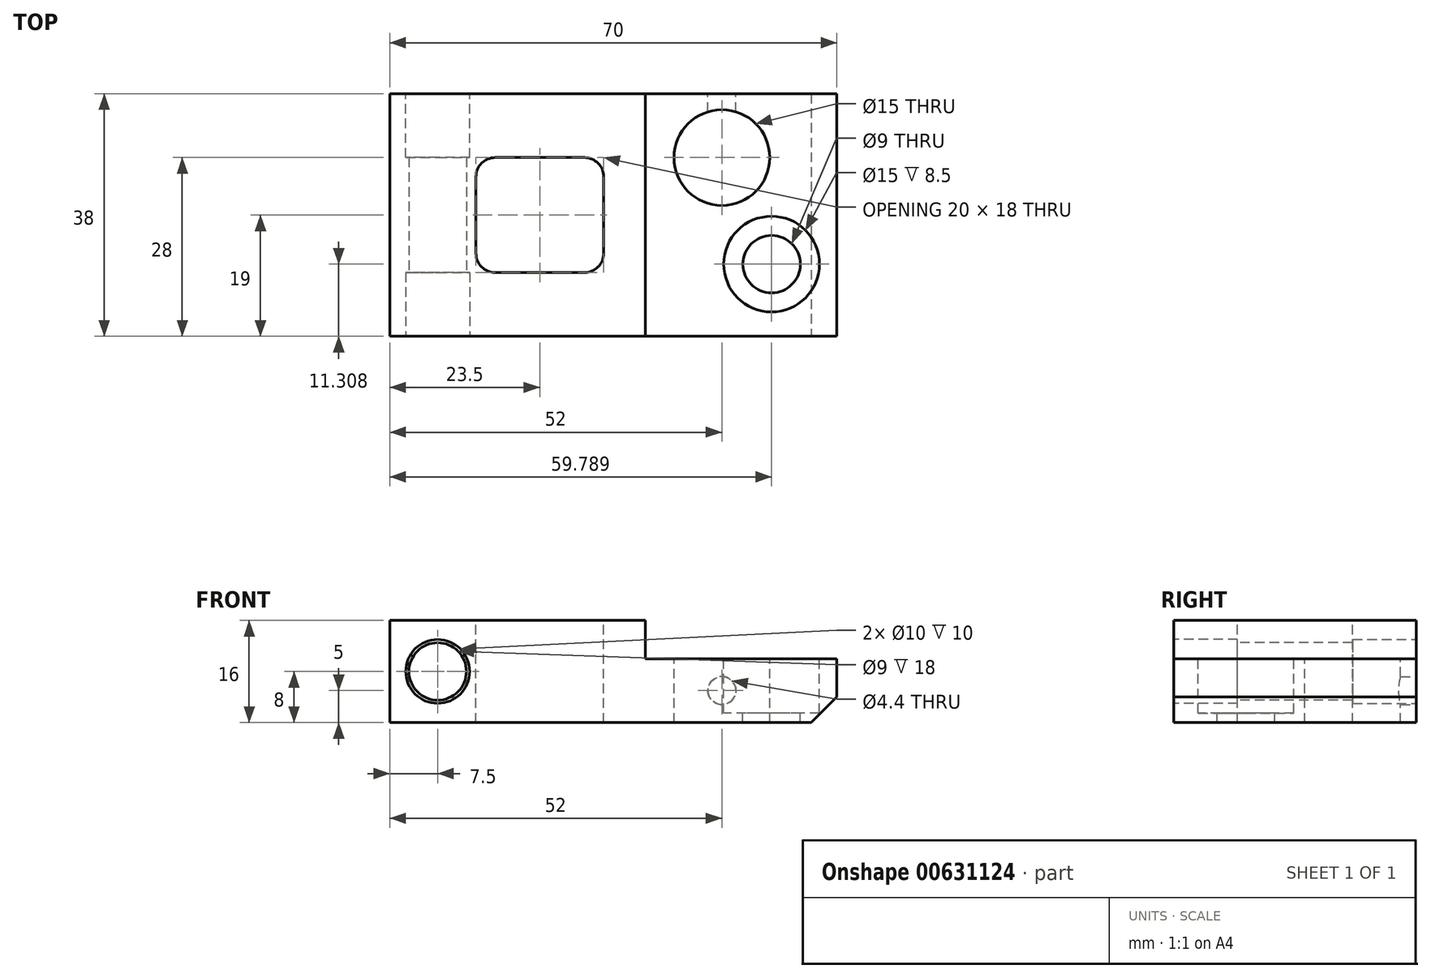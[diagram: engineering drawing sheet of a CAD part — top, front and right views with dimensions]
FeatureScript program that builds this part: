
annotation { "Feature Type Name" : "Feature", "Feature Type Description" : "" }
export const myFeature = defineFeature(function(context is Context, id is Id, definition is map)
    precondition{}
    {
        {
            var Q0;
            Q0=qCreatedBy(makeId("Top.planeOp"),FACE);
            var sketch = newSketch(context, id + "F0", { "sketchPlane" : qUnion([Q0])});
            skLineSegment(sketch, "E0.bottom", {"start": v(-35, 19) * mm, "end": v(35, 19) * mm});
            skLineSegment(sketch, "E0.top", {"start": v(-35, -19) * mm, "end": v(35, -19) * mm});
            skLineSegment(sketch, "E0.left", {"start": v(-35, 19) * mm, "end": v(-35, -19) * mm});
            skLineSegment(sketch, "E0.right", {"start": v(35, 19) * mm, "end": v(35, -19) * mm});
            skSolve(sketch);
        }
        {
            var Q0;
            Q0=makeQuery(id+"F0.imprint","IMPRINT",FACE,{"disambiguationData":[TD([[makeQuery(id+"F0.imprint","IMPRINT",EDGE,{"derivedFrom":sQuery(id+"F0.wireOp",EDGE,"E0.bottom")}),-1.0]])]});
            extrude(context, id + "F1", {"entities" : qUnion([Q0]), "depth" : 16 * mm, "offsetDistance" : 25 * mm});
        }
        {
            var Q0;
            Q0=makeQuery(id+"F1.opExtrude","SWEPT_FACE",FACE,{"disambiguationData":[OSD([sQuery(id+"F0.wireOp",EDGE,"E0.top")])]});
            var sketch = newSketch(context, id + "F2", { "sketchPlane" : qUnion([Q0])});
            skPoint(sketch, "E1", {"position": v(-27.5, 8) * mm});
            skSolve(sketch);
        }
        {
            var Q0;
            Q0=sQuery(id+"F2.wireOp",VERTEX,"E1");
            var Q1;
            Q1=makeQuery(id+"F1.opExtrude","SWEPT_BODY",BODY,{"disambiguationData":[OSD([sQuery(id+"F0.wireOp",EDGE,"E0.bottom"),sQuery(id+"F0.wireOp",EDGE,"E0.top"),sQuery(id+"F0.wireOp",EDGE,"E0.left"),sQuery(id+"F0.wireOp",EDGE,"E0.right")])]});
            hole(context, id + "F3", {"style" : HoleStyle.C_BORE, "endStyle" : HoleEndStyle.BLIND, "holeDiameter" : 9 * mm, "cBoreDiameter" : 10 * mm, "cBoreDepth" : 10 * mm, "majorDiameter" : 4 * mm, "holeDepth" : 28 * mm, "isTappedThrough" : true, "tappedDepth" : 11.5 * mm, "tapClearance" : 3, "locations" : qUnion([Q0]), "scope" : qUnion([Q1])});
        }
        {
            var Q0;
            Q0=makeQuery(id+"F1.opExtrude","SWEPT_FACE",FACE,{"disambiguationData":[OSD([sQuery(id+"F0.wireOp",EDGE,"E0.bottom")])]});
            var sketch = newSketch(context, id + "F4", { "sketchPlane" : qUnion([Q0])});
            skPoint(sketch, "E2", {"position": v(27.5, 8) * mm});
            skSolve(sketch);
        }
        {
            var Q0;
            Q0=sQuery(id+"F4.wireOp",VERTEX,"E2");
            var Q1;
            Q1=makeQuery(id+"F1.opExtrude","SWEPT_BODY",BODY,{"disambiguationData":[OSD([sQuery(id+"F0.wireOp",EDGE,"E0.bottom"),sQuery(id+"F0.wireOp",EDGE,"E0.top"),sQuery(id+"F0.wireOp",EDGE,"E0.left"),sQuery(id+"F0.wireOp",EDGE,"E0.right")])]});
            hole(context, id + "F5", {"style" : HoleStyle.C_BORE, "endStyle" : HoleEndStyle.BLIND, "holeDiameter" : 9 * mm, "cBoreDiameter" : 10 * mm, "cBoreDepth" : 10 * mm, "majorDiameter" : 5 * mm, "holeDepth" : 28 * mm, "isTappedThrough" : true, "tappedDepth" : 11.5 * mm, "tapClearance" : 3, "locations" : qUnion([Q0]), "scope" : qUnion([Q1])});
        }
        {
            var Q0;
            Q0=makeQuery(id+"F1.opExtrude","CAP_FACE",FACE,{"disambiguationData":[OSD([sQuery(id+"F0.wireOp",EDGE,"E0.bottom"),sQuery(id+"F0.wireOp",EDGE,"E0.top"),sQuery(id+"F0.wireOp",EDGE,"E0.left"),sQuery(id+"F0.wireOp",EDGE,"E0.right")])],"isStart":false});
            var sketch = newSketch(context, id + "F6", { "sketchPlane" : qUnion([Q0])});
            skLineSegment(sketch, "E3.bottom", {"start": v(-18.5, 9) * mm, "end": v(-4.5, 9) * mm});
            skLineSegment(sketch, "E3.top", {"start": v(-18.5, -9) * mm, "end": v(-4.5, -9) * mm});
            skLineSegment(sketch, "E3.left", {"start": v(-21.5, 6) * mm, "end": v(-21.5, -6) * mm});
            skLineSegment(sketch, "E3.right", {"start": v(-1.5, 6) * mm, "end": v(-1.5, -6) * mm});
            skPoint(sketch, "E4.visualSharp", {"position": v(-21.5, 9) * mm});
            skArc(sketch, "E4.filletArc", {"start": v(-18.5, 9) * mm, "mid": v(-20.62, 8.12) * mm, "end": v(-21.5, 6) * mm});
            skPoint(sketch, "E5.visualSharp", {"position": v(-21.5, -9) * mm});
            skArc(sketch, "E5.filletArc", {"start": v(-21.5, -6) * mm, "mid": v(-20.62, -8.12) * mm, "end": v(-18.5, -9) * mm});
            skPoint(sketch, "E6.visualSharp", {"position": v(-1.5, 9) * mm});
            skArc(sketch, "E6.filletArc", {"start": v(-1.5, 6) * mm, "mid": v(-2.38, 8.12) * mm, "end": v(-4.5, 9) * mm});
            skPoint(sketch, "E7.visualSharp", {"position": v(-1.5, -9) * mm});
            skArc(sketch, "E7.filletArc", {"start": v(-4.5, -9) * mm, "mid": v(-2.38, -8.12) * mm, "end": v(-1.5, -6) * mm});
            skSolve(sketch);
        }
        {
            var Q0;
            Q0 = qSketchRegion(id + "F6", true);
            extrude(context, id + "F7", {"entities" : qUnion([Q0]), "operationType" : NewBodyOperationType.REMOVE, "oppositeDirection" : true, "depth" : 25 * mm, "offsetDistance" : 25 * mm});
        }
        {
            var Q0;
            Q0=makeQuery(id+"F1.opExtrude","CAP_FACE",FACE,{"disambiguationData":[OSD([sQuery(id+"F0.wireOp",EDGE,"E0.bottom"),sQuery(id+"F0.wireOp",EDGE,"E0.top"),sQuery(id+"F0.wireOp",EDGE,"E0.left"),sQuery(id+"F0.wireOp",EDGE,"E0.right")])],"isStart":false});
            var sketch = newSketch(context, id + "F8", { "sketchPlane" : qUnion([Q0])});
            skLineSegment(sketch, "E8.bottom", {"start": v(5, 19) * mm, "end": v(35, 19) * mm});
            skLineSegment(sketch, "E8.top", {"start": v(5, -19) * mm, "end": v(35, -19) * mm});
            skLineSegment(sketch, "E8.left", {"start": v(5, 19) * mm, "end": v(5, -19) * mm});
            skLineSegment(sketch, "E8.right", {"start": v(35, 19) * mm, "end": v(35, -19) * mm});
            skSolve(sketch);
        }
        {
            var Q0;
            Q0 = qSketchRegion(id + "F8", true);
            extrude(context, id + "F9", {"entities" : qUnion([Q0]), "operationType" : NewBodyOperationType.REMOVE, "oppositeDirection" : true, "depth" : 6 * mm, "offsetDistance" : 25 * mm});
        }
        {
            var Q0;
            Q0=makeQuery(id+"F1.opExtrude","CAP_EDGE",EDGE,{"disambiguationData":[OSD([sQuery(id+"F0.wireOp",EDGE,"E0.right")])],"isStart":true});
            chamfer(context, id + "F10", {"entities" : qUnion([Q0]), "width" : 4 * mm, "tangentPropagation" : true});
        }
        {
            var Q0;
            Q0=makeQuery(id+"F9.boolean.opBoolean","COPY",FACE,{"derivedFrom":makeQuery(id+"F9.opExtrude","CAP_FACE",FACE,{"disambiguationData":[OSD([sQuery(id+"F8.wireOp",EDGE,"E8.bottom"),sQuery(id+"F8.wireOp",EDGE,"E8.top"),sQuery(id+"F8.wireOp",EDGE,"E8.left"),sQuery(id+"F8.wireOp",EDGE,"E8.right")])],"isStart":false})});
            var sketch = newSketch(context, id + "F11", { "sketchPlane" : qUnion([Q0])});
            skPoint(sketch, "E9", {"position": v(24.79, -7.7) * mm});
            skSolve(sketch);
        }
        {
            var Q0;
            Q0=sQuery(id+"F11.wireOp",VERTEX,"E9");
            var Q1;
            Q1=makeQuery(id+"F1.opExtrude","SWEPT_BODY",BODY,{"disambiguationData":[OSD([sQuery(id+"F0.wireOp",EDGE,"E0.bottom"),sQuery(id+"F0.wireOp",EDGE,"E0.top"),sQuery(id+"F0.wireOp",EDGE,"E0.left"),sQuery(id+"F0.wireOp",EDGE,"E0.right")])]});
            hole(context, id + "F12", {"style" : HoleStyle.C_BORE, "endStyle" : HoleEndStyle.BLIND, "holeDiameter" : 9 * mm, "cBoreDiameter" : 15 * mm, "cBoreDepth" : 8.5 * mm, "majorDiameter" : 5 * mm, "holeDepth" : 28 * mm, "isTappedThrough" : true, "tappedDepth" : 11.5 * mm, "tapClearance" : 3, "locations" : qUnion([Q0]), "scope" : qUnion([Q1])});
        }
        {
            var Q0;
            Q0=makeQuery(id+"F9.boolean.opBoolean","COPY",FACE,{"derivedFrom":makeQuery(id+"F9.opExtrude","CAP_FACE",FACE,{"disambiguationData":[OSD([sQuery(id+"F8.wireOp",EDGE,"E8.bottom"),sQuery(id+"F8.wireOp",EDGE,"E8.top"),sQuery(id+"F8.wireOp",EDGE,"E8.left"),sQuery(id+"F8.wireOp",EDGE,"E8.right")])],"isStart":false})});
            var sketch = newSketch(context, id + "F13", { "sketchPlane" : qUnion([Q0])});
            skPoint(sketch, "E10", {"position": v(17, 9) * mm});
            skSolve(sketch);
        }
        {
            var Q0;
            Q0=sQuery(id+"F13.wireOp",VERTEX,"E10");
            var Q1;
            Q1=makeQuery(id+"F1.opExtrude","SWEPT_BODY",BODY,{"disambiguationData":[OSD([sQuery(id+"F0.wireOp",EDGE,"E0.bottom"),sQuery(id+"F0.wireOp",EDGE,"E0.top"),sQuery(id+"F0.wireOp",EDGE,"E0.left"),sQuery(id+"F0.wireOp",EDGE,"E0.right")])]});
            hole(context, id + "F14", {"style" : HoleStyle.SIMPLE, "endStyle" : HoleEndStyle.BLIND, "holeDiameter" : 15 * mm, "majorDiameter" : 5 * mm, "holeDepth" : 28 * mm, "isTappedThrough" : true, "tappedDepth" : 11.5 * mm, "tapClearance" : 3, "locations" : qUnion([Q0]), "scope" : qUnion([Q1])});
        }
        {
            var Q0;
            Q0=makeQuery(id+"F1.opExtrude","SWEPT_FACE",FACE,{"disambiguationData":[OSD([sQuery(id+"F0.wireOp",EDGE,"E0.bottom")])]});
            var sketch = newSketch(context, id + "F15", { "sketchPlane" : qUnion([Q0])});
            skPoint(sketch, "E11", {"position": v(-17, 5) * mm});
            skSolve(sketch);
        }
        {
            var Q0;
            Q0=sQuery(id+"F15.wireOp",VERTEX,"E11");
            var Q1;
            Q1=makeQuery(id+"F1.opExtrude","SWEPT_BODY",BODY,{"disambiguationData":[OSD([sQuery(id+"F0.wireOp",EDGE,"E0.bottom"),sQuery(id+"F0.wireOp",EDGE,"E0.top"),sQuery(id+"F0.wireOp",EDGE,"E0.left"),sQuery(id+"F0.wireOp",EDGE,"E0.right")])]});
            hole(context, id + "F16", {"style" : HoleStyle.SIMPLE, "endStyle" : HoleEndStyle.BLIND, "standardTappedOrClearance" : lookupTablePath({ "standard" : "ISO", "fit" : "Normal", "size" : "M4", "type" : "Clearance" }), "standardBlindInLast" : lookupTablePath({ "fit" : "Standard", "standard" : "ISO", "size" : "M4", "type" : "Clearance" }), "holeDiameter" : 4.4 * mm, "majorDiameter" : 5 * mm, "holeDepth" : 10 * mm, "isTappedThrough" : true, "tappedDepth" : 11.5 * mm, "tapClearance" : 3, "locations" : qUnion([Q0]), "scope" : qUnion([Q1])});
        }
    });
